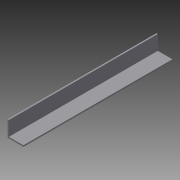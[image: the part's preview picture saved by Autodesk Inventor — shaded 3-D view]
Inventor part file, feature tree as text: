
AUTODESK INVENTOR PART (.ipt)
format: ipt  version: 2015 (Build 190159000, 159)  size: 78,336 bytes
history: native  units: in
note: dims shown in document units (in); Inventor stores cm internally (conversion verified against a paired STEP export)
features: extrude x2, sketch x2
ambient origin geometry x8: Origin, YZ Plane, XZ Plane, XY Plane, X Axis, Y Axis, Z Axis, Center Point
bodies: Solid1 (feature_tree)
feature tree (4):
  extrude  "Extrusion1"  Depth=0.125in
  extrude  "Extrusion2"  Depth=0.125in
  sketch  "Sketch1"  dims[d0=1.5in d1=0.125in]
  sketch  "Sketch2"  dims[d2=14.0in d3=0.0in d4=0.125in d5=1.5in d6=14.0in d7=0.0in]
